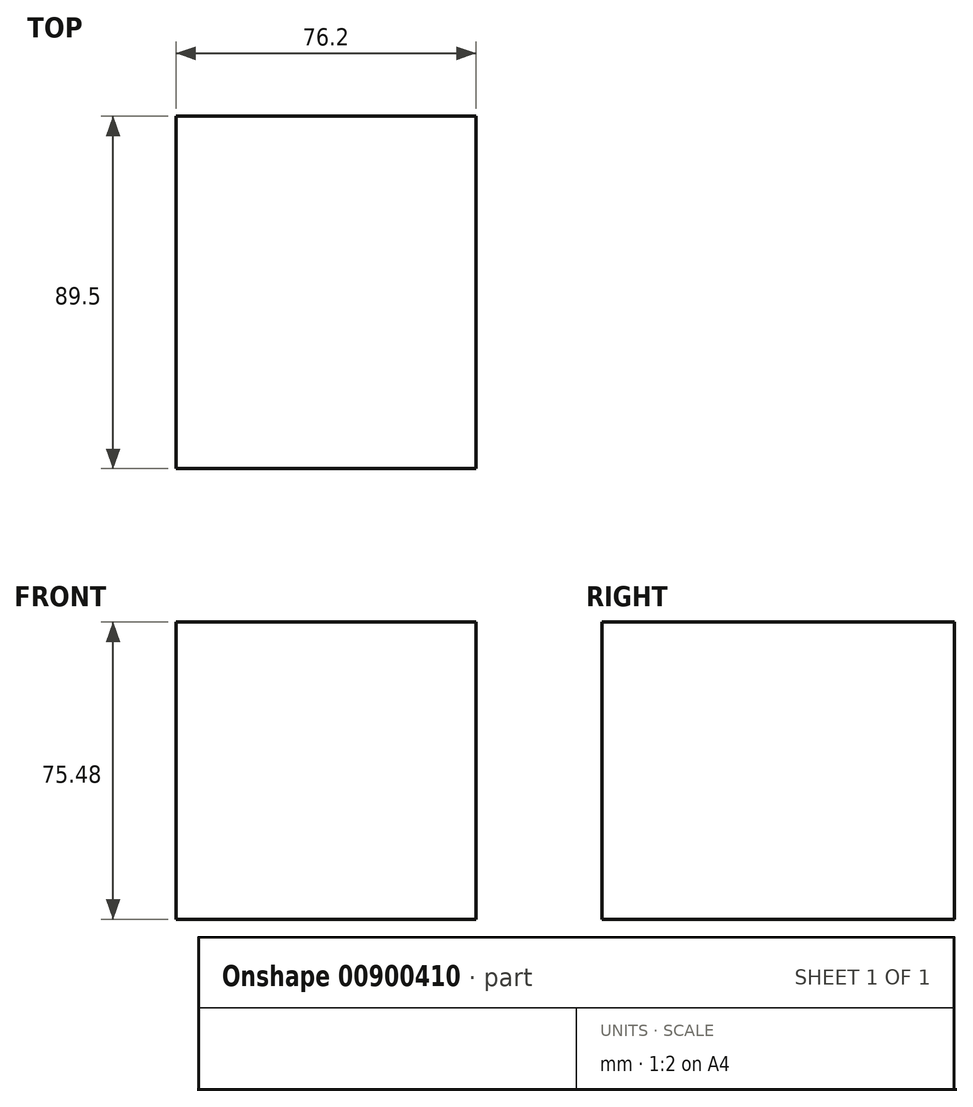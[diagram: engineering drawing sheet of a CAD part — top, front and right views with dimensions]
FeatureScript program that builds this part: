
annotation { "Feature Type Name" : "Feature", "Feature Type Description" : "" }
export const myFeature = defineFeature(function(context is Context, id is Id, definition is map)
    precondition{}
    {
        {
            var Q0;
            Q0=qCreatedBy(makeId("Right.planeOp"),FACE);
            var sketch = newSketch(context, id + "F0", { "sketchPlane" : qUnion([Q0])});
            skLineSegment(sketch, "E0.bottom", {"start": v(14.8, 0) * mm, "end": v(-74.7, 0) * mm});
            skLineSegment(sketch, "E0.top", {"start": v(14.8, 75.48) * mm, "end": v(-74.7, 75.48) * mm});
            skLineSegment(sketch, "E0.left", {"start": v(14.8, 0) * mm, "end": v(14.8, 75.48) * mm});
            skLineSegment(sketch, "E0.right", {"start": v(-74.7, 0) * mm, "end": v(-74.7, 75.48) * mm});
            skSolve(sketch);
        }
        {
            var Q0;
            Q0=makeQuery(id+"F0.imprint","IMPRINT",FACE,{"disambiguationData":[TD([[makeQuery(id+"F0.imprint","IMPRINT",EDGE,{"derivedFrom":sQuery(id+"F0.wireOp",EDGE,"E0.bottom")}),-1.0]])]});
            extrude(context, id + "F1", {"entities" : qUnion([Q0]), "depth" : 76.2 * mm, "offsetDistance" : 25.4 * mm});
        }
    });
